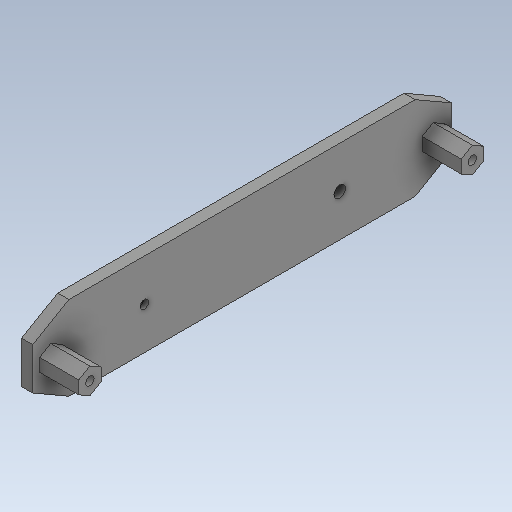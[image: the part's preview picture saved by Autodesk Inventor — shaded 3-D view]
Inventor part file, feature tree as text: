
AUTODESK INVENTOR PART (.ipt)
format: ipt  version: 2020 (Build 240168000, 168)  size: 238,080 bytes
history: native  units: in
note: dims shown in document units (in); Inventor stores cm internally (conversion verified against a paired STEP export)
features: extrude x7, sketch x7, plane x1
ambient origin geometry x8: Origin, YZ Plane, XZ Plane, XY Plane, X Axis, Y Axis, Z Axis, Center Point
bodies: Solid1 (feature_tree)
feature tree (15):
  extrude  "Extrusion1"  Depth=5.9055in
  extrude  "Extrusion3"  TaperAngle=0.0deg  [1 undecoded]
  extrude  "Extrusion4"  Depth=0.5512in
  plane  "Work Plane1"
  extrude  "Extrusion5"  Depth=0.122in
  extrude  "Extrusion6"  Depth=0.2402in
  extrude  "Extrusion7"  [1 undecoded]
  extrude  "Extrusion8"  Depth=0.0866in TaperAngle=0.0deg
  sketch  "Sketch1"  dims[d0=1.1811in d1=5.9055in]
  sketch  "Sketch2"  dims[d2=0.1575in d3=0.0in]
  sketch  "Sketch3"  dims[d8=0.315in d9=0.5512in]
  sketch  "Sketch4"  dims[d10=0.0in d12=0.122in]
  sketch  "Sketch5"  dims[d13=0.0in d14=0.0in d15=0.2402in]
  sketch  "Sketch8"  dims[d16=0.0866in d17=-0.2233in]
  sketch  "Sketch9"  dims[d18=-0.3937in d19=0.0866in d20=0.0in d26=1.5748in d27=0.1654in d28=0.122in d29=1.5748in d30=0.0in d31=0.0in d32=0.2402in d33=0.0866in d34=-0.2233in]
note: 2 required parameter values undecoded (feature->parameter linkage not recoverable at this tier; creation-order binding heuristic only, values carry confidence <= 0.55)
